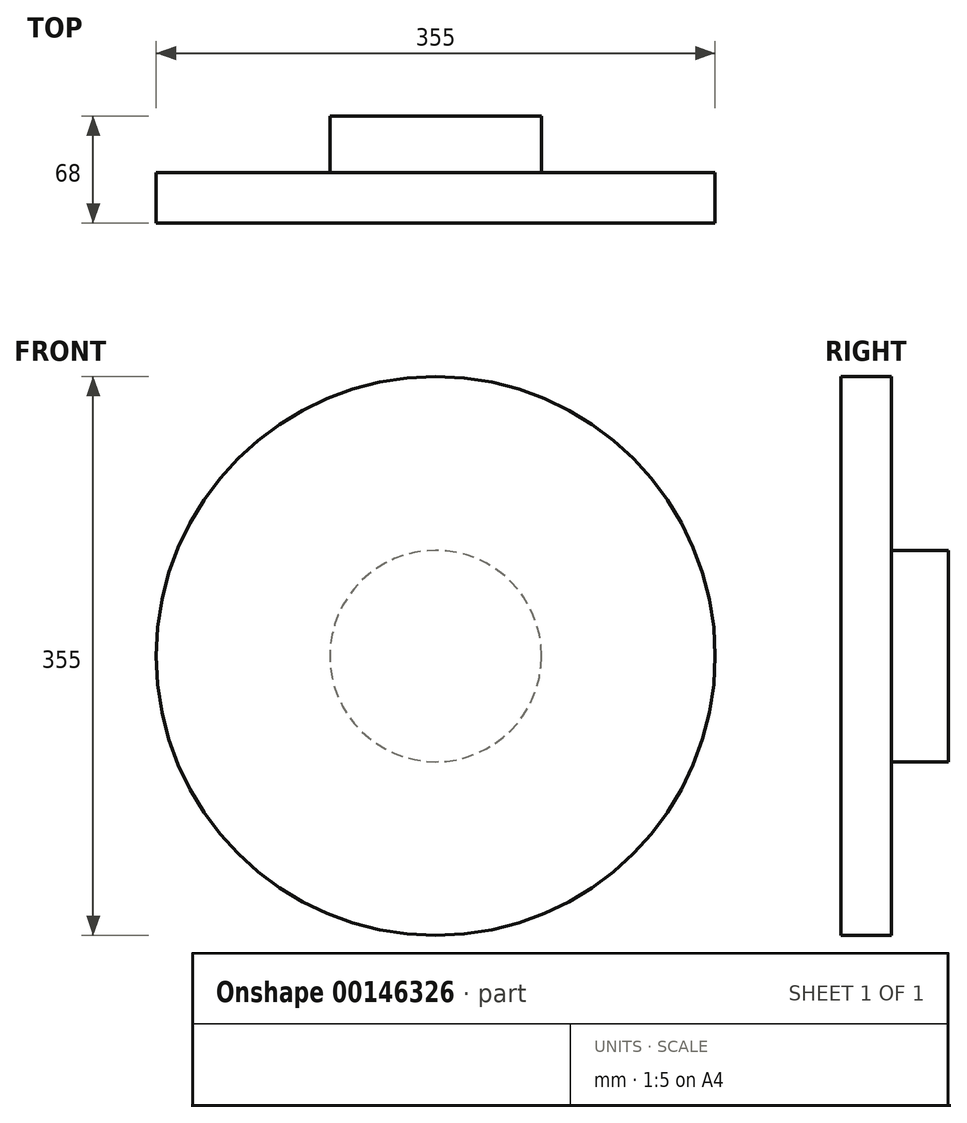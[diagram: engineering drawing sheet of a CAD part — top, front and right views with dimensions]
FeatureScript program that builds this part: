
annotation { "Feature Type Name" : "Feature", "Feature Type Description" : "" }
export const myFeature = defineFeature(function(context is Context, id is Id, definition is map)
    precondition{}
    {
        {
            var Q0;
            Q0=qCreatedBy(makeId("Right.planeOp"),FACE);
            var sketch = newSketch(context, id + "F0", { "sketchPlane" : qUnion([Q0])});
            skLineSegment(sketch, "E0", {"start": v(0, 0) * mm, "end": v(-68, 0) * mm, "construction": true});
            skLineSegment(sketch, "E1", {"start": v(-68, 0) * mm, "end": v(-68, 177.5) * mm});
            skLineSegment(sketch, "E2", {"start": v(-68, 177.5) * mm, "end": v(-36, 177.5) * mm});
            skLineSegment(sketch, "E3", {"start": v(-36, 177.5) * mm, "end": v(-36, 67.15) * mm});
            skLineSegment(sketch, "E4", {"start": v(-36, 67.15) * mm, "end": v(0, 67.15) * mm});
            skLineSegment(sketch, "E5", {"start": v(0, 67.15) * mm, "end": v(0, 0) * mm});
            skLineSegment(sketch, "E6", {"start": v(0, 0) * mm, "end": v(-68, 0) * mm});
            skSolve(sketch);
        }
        {
            var Q0;
            Q0 = qSketchRegion(id + "F0", true);
            var Q1;
            Q1=sQuery(id+"F0.wireOp",EDGE,"E6");
            revolve(context, id + "F1", {"entities" : qUnion([Q0]), "axis" : qUnion([Q1]), "revolveType" : RevolveType.FULL});
        }
    });
